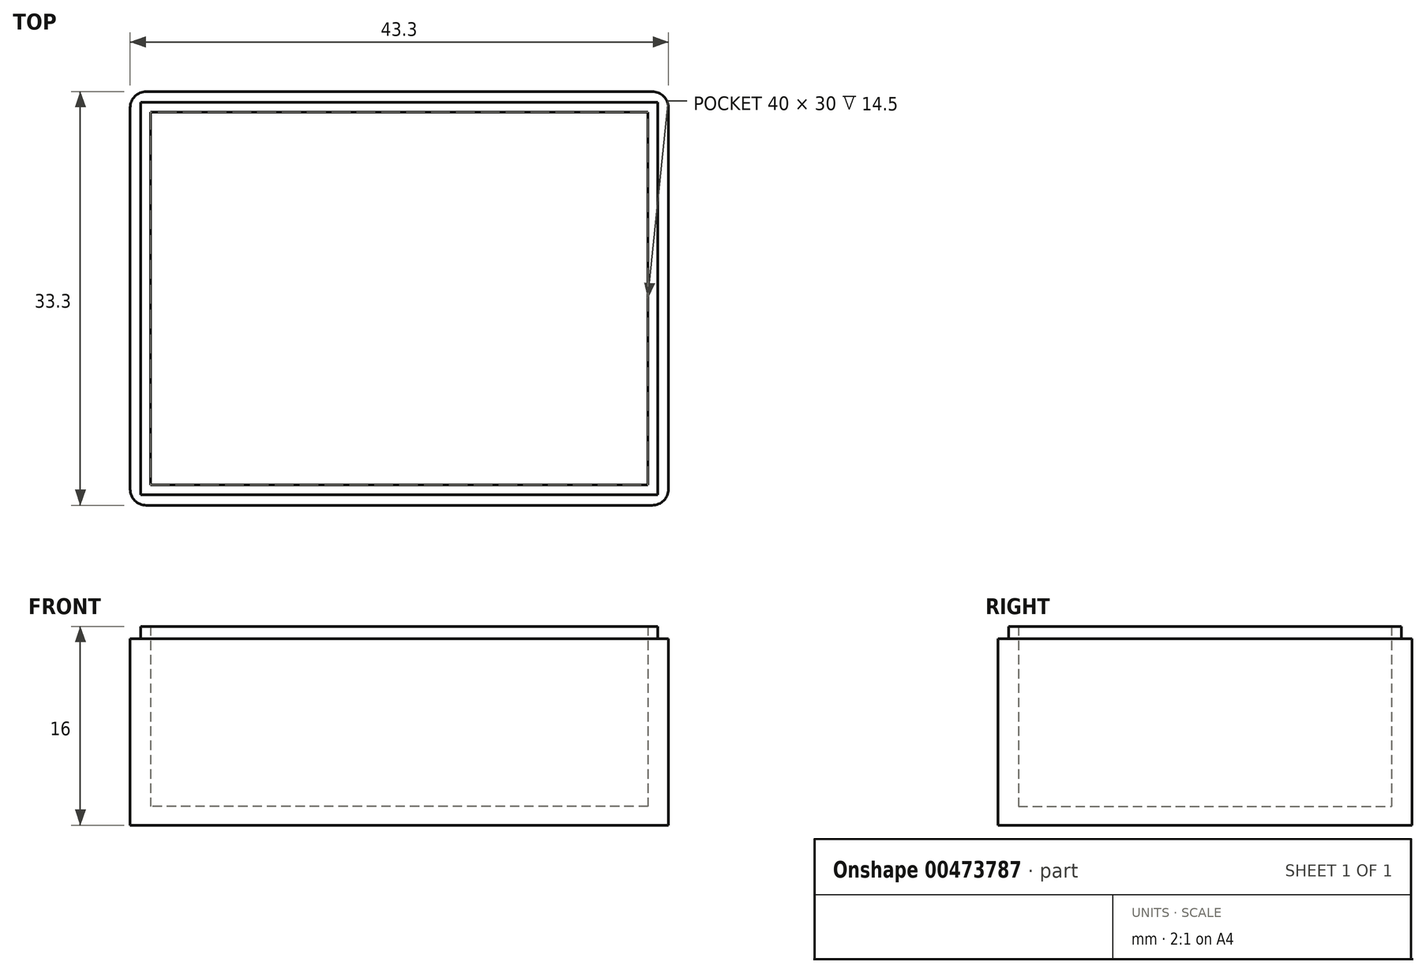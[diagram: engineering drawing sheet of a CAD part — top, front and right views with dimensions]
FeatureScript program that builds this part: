
annotation { "Feature Type Name" : "Feature", "Feature Type Description" : "" }
export const myFeature = defineFeature(function(context is Context, id is Id, definition is map)
    precondition{}
    {
        {
            var Q0;
            Q0=qCreatedBy(makeId("Top.planeOp"),FACE);
            var sketch = newSketch(context, id + "F0", { "sketchPlane" : qUnion([Q0])});
            skLineSegment(sketch, "E0.bottom", {"start": v(20, -15) * mm, "end": v(-20, -15) * mm});
            skLineSegment(sketch, "E0.top", {"start": v(20, 15) * mm, "end": v(-20, 15) * mm});
            skLineSegment(sketch, "E0.left", {"start": v(20, -15) * mm, "end": v(20, 15) * mm});
            skLineSegment(sketch, "E0.right", {"start": v(-20, -15) * mm, "end": v(-20, 15) * mm});
            skPoint(sketch, "E0.middle", {"position": v(0, 0) * mm});
            skLineSegment(sketch, "E1.0", {"start": v(21.65, -16.65) * mm, "end": v(-21.65, -16.65) * mm});
            skLineSegment(sketch, "E1.1", {"start": v(21.65, -16.65) * mm, "end": v(21.65, 16.65) * mm});
            skLineSegment(sketch, "E1.2", {"start": v(21.65, 16.65) * mm, "end": v(-21.65, 16.65) * mm});
            skLineSegment(sketch, "E1.3", {"start": v(-21.65, -16.65) * mm, "end": v(-21.65, 16.65) * mm});
            skSolve(sketch);
        }
        {
            var Q0;
            Q0=makeQuery(id+"F0.imprint","IMPRINT",FACE,{"disambiguationData":[TD([[makeQuery(id+"F0.imprint","IMPRINT",EDGE,{"derivedFrom":sQuery(id+"F0.wireOp",EDGE,"E0.bottom")}),1.0]])]});
            extrude(context, id + "F1", {"entities" : qUnion([Q0]), "depth" : 15 * mm});
        }
        {
            var Q0;
            Q0=makeQuery(id+"F0.imprint","IMPRINT",FACE,{"disambiguationData":[TD([[makeQuery(id+"F0.imprint","IMPRINT",EDGE,{"derivedFrom":sQuery(id+"F0.wireOp",EDGE,"E0.bottom")}),-1.0]])]});
            extrude(context, id + "F2", {"entities" : qUnion([Q0]), "operationType" : NewBodyOperationType.ADD, "depth" : 1.5 * mm});
        }
        {
            var Q0;
            Q0=makeQuery(id+"F1.opExtrude","CAP_FACE",FACE,{"disambiguationData":[OSD([sQuery(id+"F0.wireOp",EDGE,"E0.bottom"),sQuery(id+"F0.wireOp",EDGE,"E0.top"),sQuery(id+"F0.wireOp",EDGE,"E0.left"),sQuery(id+"F0.wireOp",EDGE,"E0.right"),sQuery(id+"F0.wireOp",EDGE,"E1.0"),sQuery(id+"F0.wireOp",EDGE,"E1.1"),sQuery(id+"F0.wireOp",EDGE,"E1.2"),sQuery(id+"F0.wireOp",EDGE,"E1.3")])],"isStart":false});
            var sketch = newSketch(context, id + "F3", { "sketchPlane" : qUnion([Q0])});
            skLineSegment(sketch, "E2.0", {"start": v(-20.8, -15.8) * mm, "end": v(-20.8, 15.8) * mm});
            skLineSegment(sketch, "E2.1", {"start": v(20.8, -15.8) * mm, "end": v(-20.8, -15.8) * mm});
            skLineSegment(sketch, "E2.2", {"start": v(20.8, -15.8) * mm, "end": v(20.8, 15.8) * mm});
            skLineSegment(sketch, "E2.3", {"start": v(20.8, 15.8) * mm, "end": v(-20.8, 15.8) * mm});
            skLineSegment(sketch, "E3", {"start": v(-20, -15) * mm, "end": v(-20, 15) * mm});
            skLineSegment(sketch, "E4", {"start": v(-20, 15) * mm, "end": v(20, 15) * mm});
            skLineSegment(sketch, "E5", {"start": v(20, 15) * mm, "end": v(20, -15) * mm});
            skLineSegment(sketch, "E6", {"start": v(20, -15) * mm, "end": v(-20, -15) * mm});
            skSolve(sketch);
        }
        {
            var Q0;
            Q0=qSketchRegion(id+"F3",true);
            extrude(context, id + "F4", {"entities" : qUnion([Q0]), "operationType" : NewBodyOperationType.ADD, "depth" : 1 * mm});
        }
        {
            var Q0;
            Q0=makeQuery(id+"F1.opExtrude","SWEPT_EDGE",EDGE,{"disambiguationData":[OSD([sQuery(id+"F0.wireOp",EDGE,"E1.0"),sQuery(id+"F0.wireOp",EDGE,"E1.3")])]});
            var Q1;
            Q1=makeQuery(id+"F1.opExtrude","SWEPT_EDGE",EDGE,{"disambiguationData":[OSD([sQuery(id+"F0.wireOp",EDGE,"E1.0"),sQuery(id+"F0.wireOp",EDGE,"E1.1")])]});
            var Q2;
            Q2=makeQuery(id+"F1.opExtrude","SWEPT_EDGE",EDGE,{"disambiguationData":[OSD([sQuery(id+"F0.wireOp",EDGE,"E1.1"),sQuery(id+"F0.wireOp",EDGE,"E1.2")])]});
            var Q3;
            Q3=makeQuery(id+"F1.opExtrude","SWEPT_EDGE",EDGE,{"disambiguationData":[OSD([sQuery(id+"F0.wireOp",EDGE,"E1.2"),sQuery(id+"F0.wireOp",EDGE,"E1.3")])]});
            fillet(context, id + "F5", {"entities" : qUnion([Q0, Q1, Q2, Q3]), "radius" : 1.3 * mm, "tangentPropagation" : true, "allowEdgeOverflow" : false});
        }
    });
